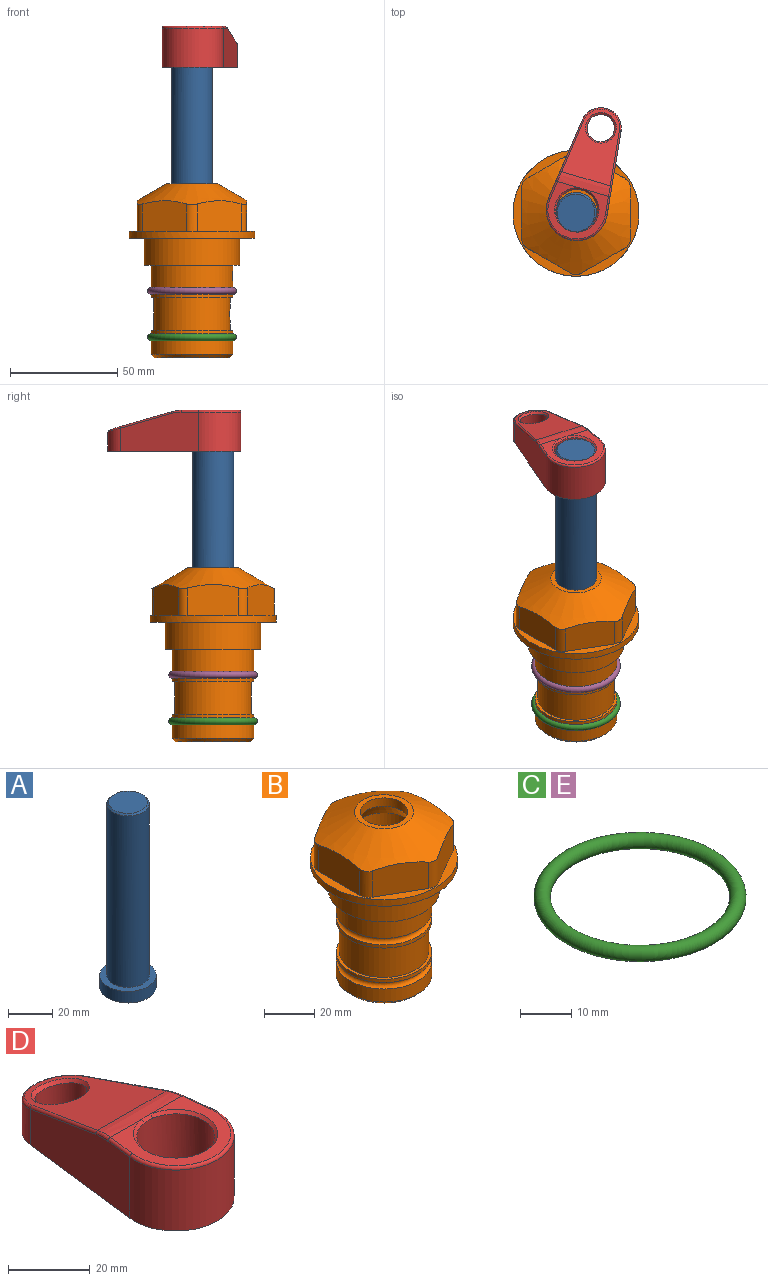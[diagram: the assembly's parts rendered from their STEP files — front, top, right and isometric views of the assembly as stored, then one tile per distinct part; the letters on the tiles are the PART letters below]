
ASSEMBLY  parts=5 mates=3
PART A: 6 faces, bbox 25.4x25.4x101.6 mm
  f0: plane 17.46x17.46mm, normal (0,0,1), area 239.5mm2, adj f5
  f1: plane 25.4x25.4mm, normal (0,0,-1), area 506.7mm2, adj f2
  f2: cylinder r=12.7mm len=25.4mm, axis (0,0,1), area 506.7mm2, adj f1,f3
  f3: plane 25.4x25.4mm, normal (0,0,1), area 221.7mm2, adj f2,f4
  f4: cylinder r=9.53mm len=94.46mm, axis (0,0,1), area 5653mm2, adj f3,f5
  f5: cone r=8.73mm half-angle=45deg, axis (0,0,-1), area 64.4mm2, adj f0,f4
PART B: 36 faces, bbox 58.7x58.7x81 mm
  f0: cylinder r=17.78mm len=35.56mm, axis (0,0,1), area 1670.8mm2, adj f23,f24,f31
  f1: cylinder r=19.05mm len=38.1mm, axis (0,0,1), area 1191.9mm2, adj f26,f27,f30
  f2: plane 58.66x58.66mm, normal (0,0,-1), area 1150.6mm2, adj f3,f28
  f3: cylinder r=29.33mm len=58.66mm, axis (0,0,-1), area 585.1mm2, adj f2,f4
  f4: plane 58.66x58.66mm, normal (0,0,1), area 475.9mm2, adj f3,f5,f6,f7,f8,f9,f10,f11
  f5: plane 20.32x14.34mm, normal (-0.5,0.87,0), area 324.4mm2, adj f4,f15,f16,f17
  f6: plane 20.32x14.34mm, normal (0.5,0.87,0), area 324.4mm2, adj f4,f14,f15,f17
  f7: plane 23.48x14.34mm, normal (1,0,0), area 324.4mm2, adj f4,f13,f14,f17
  f8: plane 20.32x14.34mm, normal (0.5,-0.87,0), area 324.4mm2, adj f4,f12,f13,f17
  f9: plane 20.32x14.34mm, normal (-0.5,-0.87,0), area 324.4mm2, adj f4,f11,f12,f17
  f10: plane 23.48x14.34mm, normal (-1,0,0), area 324.4mm2, adj f4,f11,f16,f17
  f11: cylinder r=5.08mm len=12.85mm, axis (0,0,-1), area 67.2mm2, adj f4,f9,f10,f17
  f12: cylinder r=5.08mm len=12.85mm, axis (0,0,-1), area 67.2mm2, adj f4,f8,f9,f17
  f13: cylinder r=5.08mm len=12.85mm, axis (0,0,-1), area 67.2mm2, adj f4,f7,f8,f17
  f14: cylinder r=5.08mm len=12.85mm, axis (0,0,-1), area 67.2mm2, adj f4,f6,f7,f17
  f15: cylinder r=5.08mm len=12.85mm, axis (0,0,-1), area 67.2mm2, adj f4,f5,f6,f17
  f16: cylinder r=5.08mm len=12.85mm, axis (0,0,-1), area 67.2mm2, adj f4,f5,f10,f17
  f17: cone r=11.73mm half-angle=60deg, axis (0,0,-1), area 2071.8mm2, adj f5,f6,f7,f8,f9,f10,f11,f12
  f18: plane 23.46x23.46mm, normal (0,0,1), area 147.4mm2, adj f17,f35
  f19: plane 34.93x34.93mm, normal (0,0,-1), area 958mm2, adj f29
  f20: cylinder r=19.05mm len=38.1mm, axis (0,0,1), area 760.1mm2, adj f21,f29
  f21: torus R=19.05mm, axis (0,0,1), area 565.3mm2, adj f20,f22
  f22: cylinder r=19.05mm len=38.1mm, axis (0,0,1), area 190mm2, adj f21,f23
  f23: plane 38.1x38.1mm, normal (0,0,1), area 146.9mm2, adj f0,f22
  f24: plane 38.1x38.1mm, normal (0,0,-1), area 146.9mm2, adj f0,f25
  f25: cylinder r=19.05mm len=38.1mm, axis (0,0,1), area 190mm2, adj f24,f26
  f26: torus R=19.05mm, axis (0,0,1), area 565.3mm2, adj f1,f25
  f27: plane 44.45x44.45mm, normal (0,0,-1), area 411.7mm2, adj f1,f28
  f28: cylinder r=22.23mm len=44.45mm, axis (0,0,1), area 1773.5mm2, adj f2,f27
  f29: cone r=19.05mm half-angle=45deg, axis (0,0,1), area 257.5mm2, adj f19,f20
  f30: cylinder r=3.17mm len=6.75mm, axis (-1,0,0), area 128mm2, adj f1,f33
  f31: cylinder r=3.17mm len=6.35mm, axis (-1,0,0), area 102.5mm2, adj f0,f33
  f32: plane 25.4x25.4mm, normal (0,0,1), area 506.7mm2, adj f33
  f33: cylinder r=12.7mm len=66.42mm, axis (0,0,-1), area 5236.2mm2, adj f30,f31,f32,f34
  f34: cone r=9.53mm half-angle=30deg, axis (0,0,-1), area 443.4mm2, adj f33,f35
  f35: cylinder r=9.53mm len=19.05mm, axis (0,0,-1), area 240.9mm2, adj f18,f34
PART C: 1 faces, bbox 44.7x44.7x3.2 mm
  f0: torus R=19.05mm, axis (0,0,1), area 1193.9mm2
PART D: 31 faces, bbox 31.7x65.5x19.8 mm
  f0: plane 39.12x18.26mm, normal (0.99,0.12,0), area 612.2mm2, adj f1,f4,f7,f11,f13,f15
  f1: cylinder r=9.53mm len=18.91mm, axis (0,0,-1), area 296.1mm2, adj f0,f2,f7,f17
  f2: plane 39.12x18.26mm, normal (-0.99,0.12,0), area 612.2mm2, adj f1,f4,f7,f12,f14,f16
  f3: cylinder r=6.35mm len=12.7mm, axis (0,0,-1), area 362.4mm2, adj f7,f18
  f4: cylinder r=14.29mm len=28.58mm, axis (0,0,-1), area 882.2mm2, adj f0,f2,f7,f10
  f5: cylinder r=9.53mm len=19.05mm, axis (0,0,-1), area 1092.6mm2, adj f7,f19,f20
  f6: plane 26.99x23.69mm, normal (0,0,1), area 216.2mm2, adj f9,f10,f11,f12,f19
  f7: plane 63.5x28.58mm, normal (0,0,-1), area 661.8mm2, adj f0,f1,f2,f3,f4,f5,f22,f23
  f8: plane 33.52x23.6mm, normal (0,0.26,0.97), area 486mm2, adj f9,f15,f16,f17,f18
  f9: cylinder r=19.05mm len=24.72mm, axis (1,0,0), area 120.4mm2, adj f6,f8,f13,f14,f20
  f10: torus R=13.49mm, axis (0,0,1), area 59mm2, adj f4,f6,f11,f12
  f11: cylinder r=0.79mm len=8.67mm, axis (0.12,-0.99,0), area 10.8mm2, adj f0,f6,f10,f13
  f12: cylinder r=0.79mm len=8.67mm, axis (0.12,0.99,0), area 10.8mm2, adj f2,f6,f10,f14
  f13: bspline ~4.95x1.42mm, area 6.1mm2, adj f0,f9,f11,f15
  f14: bspline ~4.95x1.42mm, area 6.1mm2, adj f2,f9,f12,f16
  f15: cylinder r=0.79mm len=25.95mm, axis (0.12,-0.96,0.26), area 32.9mm2, adj f0,f8,f13,f17
  f16: cylinder r=0.79mm len=25.95mm, axis (0.12,0.96,-0.26), area 32.9mm2, adj f2,f8,f14,f17
  f17: bspline ~18.91x8.38mm, area 30mm2, adj f1,f8,f15,f16
  f18: bspline ~14.29x14.29mm, area 48.3mm2, adj f3,f8
  f19: cone r=9.53mm half-angle=45deg, axis (0,0,1), area 66.5mm2, adj f5,f6,f20
  f20: bspline ~3.22x0.96mm, area 3.5mm2, adj f5,f9,f19
  f21: plane 2.75x2.72mm, normal (0,0,-1), area 2.9mm2, adj f23,f25,f28
  f22: plane 23.05x15.88mm, normal (-0.99,-0.12,0), area 323.6mm2, adj f7,f25,f26,f27,f28,f29
  f23: plane 23.05x15.88mm, normal (0.99,-0.12,0), area 323.6mm2, adj f7,f21,f25,f27,f28,f30
  f24: cylinder r=9.53mm len=10.69mm, axis (0,0,-1), area 114.7mm2, adj f7,f27,f29,f30
  f25: cylinder r=12.7mm len=20.59mm, axis (0,0,-1), area 381.1mm2, adj f7,f21,f22,f23,f26,f28
  f26: plane 2.75x2.72mm, normal (0,0,-1), area 2.9mm2, adj f22,f25,f28
  f27: plane 19.72x18.37mm, normal (0,-0.26,-0.97), area 291.8mm2, adj f22,f23,f24,f28,f29,f30
  f28: cylinder r=15.88mm len=19.92mm, axis (1,0,0), area 54.8mm2, adj f21,f22,f23,f25,f26,f27
  f29: cylinder r=1.59mm len=11mm, axis (0,0,-1), area 34.7mm2, adj f7,f22,f24,f27
  f30: cylinder r=1.59mm len=11mm, axis (0,0,-1), area 34.7mm2, adj f7,f23,f24,f27
PART E: same geometry as C
PLACE A rot(axis=(0,0,-1),16.3deg) t=(0,0,35.17)mm
PLACE B at identity fixed
PLACE C t=(0,0,-21.59)mm
PLACE D rot(axis=(0,0,-1),16.3deg) t=(0.4,1.37,35.17)mm
PLACE E at identity
MATE fastened D.f6 <-> A.f2  axis (0,0,1) through (0,0,98.67)mm
MATE cylindrical A.f2 <-> B.f0  axis (0,0,-1) through (0,0,-2.93)mm
MATE fastened C.f0 <-> B.f0  axis (0,0,1) through (0,0,-46.1)mm
